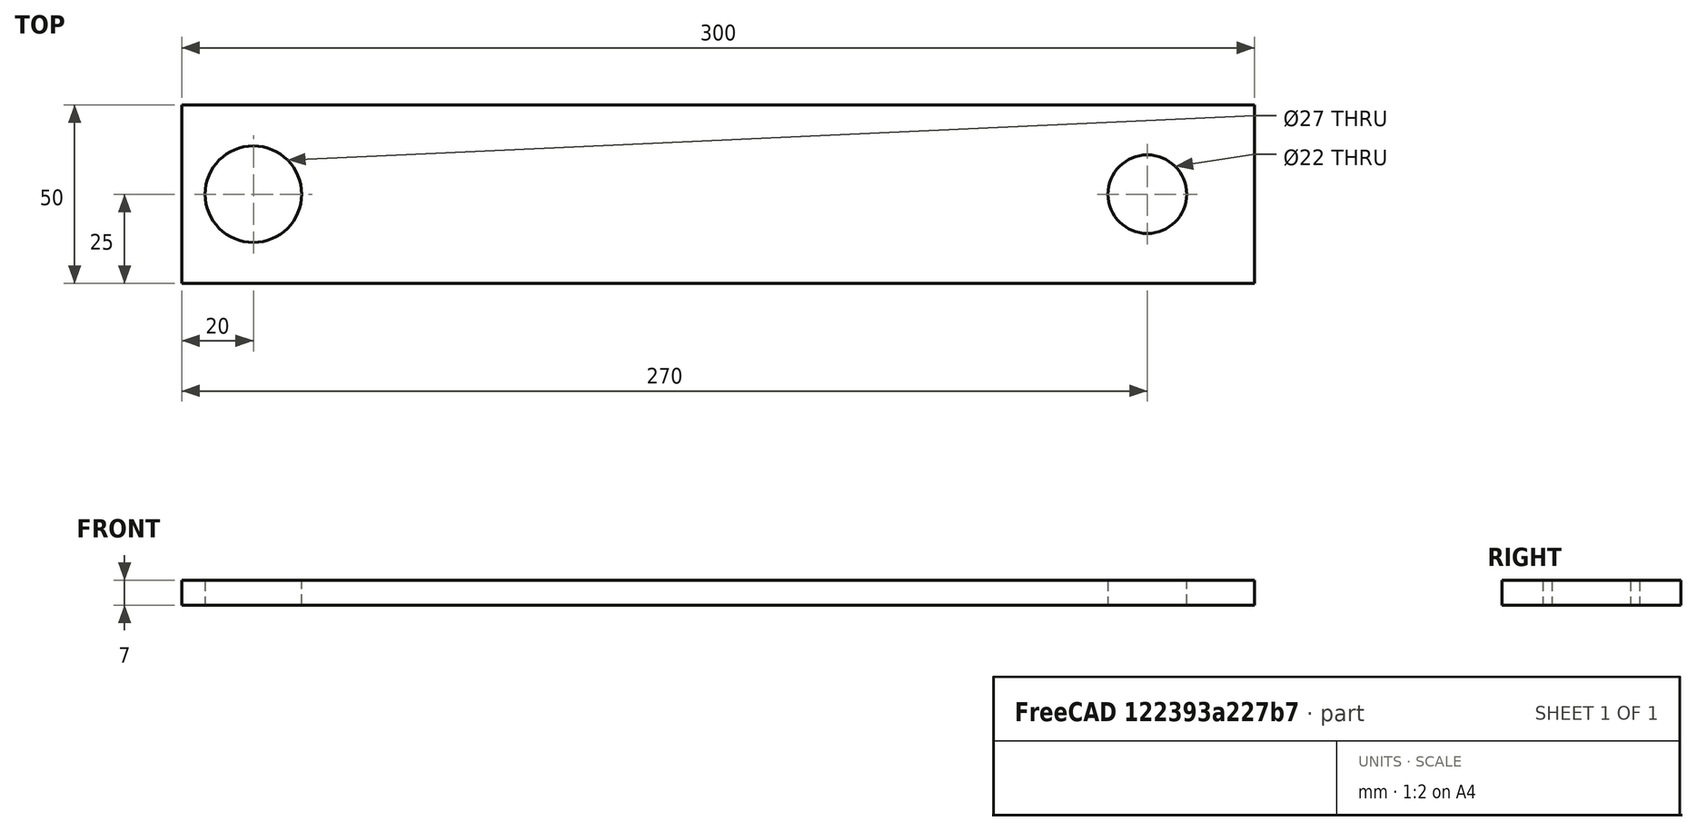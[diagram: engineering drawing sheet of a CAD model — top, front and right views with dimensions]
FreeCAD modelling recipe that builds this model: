
FCSTD DOCUMENT  (FreeCAD 0.19R24276 (Git))
Label: richag_300_d22_d27
License: All rights reserved
LicenseURL: http://en.wikipedia.org/wiki/All_rights_reserved
objects: Sketcher::SketchObject×1, PartDesign::Pad×1, PartDesign::Body×1
note: 4 computed .brp shape members not serialized (recipe doc carries the construction recipe); baked Part::Feature solids carry a one-line shape summary decoded from their .brp

FEATURE [Sketcher::SketchObject] Sketch
  FullyConstrained = true
  MapMode = 5
  Support = -> [XY_Plane]
  sketch-geometry (6):
    g0: Circle CenterX=0 CenterY=0 CenterZ=0 NormalX=0 NormalY=0 NormalZ=1 AngleXU=0 Radius=13.5
    g1: Circle CenterX=250 CenterY=0 CenterZ=0 NormalX=0 NormalY=0 NormalZ=1 AngleXU=0 Radius=11
    g2: LineSegment StartX=-20 StartY=25 StartZ=0 EndX=280 EndY=25 EndZ=0
    g3: LineSegment StartX=280 StartY=25 StartZ=0 EndX=280 EndY=-25 EndZ=0
    g4: LineSegment StartX=280 StartY=-25 StartZ=0 EndX=-20 EndY=-25 EndZ=0
    g5: LineSegment StartX=-20 StartY=-25 StartZ=0 EndX=-20 EndY=25 EndZ=0
  constraints (17):
    c: Coincident(g-1,g0)
    c: Diameter(g0) = 27
    c: PointOnObject(g1,g-1)
    c: Diameter(g1) = 22
    c: Coincident(g2,g3)
    c: Coincident(g3,g4)
    c: Coincident(g4,g5)
    c: Coincident(g5,g2)
    c: Horizontal(g2)
    c: Horizontal(g4)
    c: Vertical(g3)
    c: Vertical(g5)
    c: DistanceX(g4,g0) = 20
    c: DistanceX(g0,g1) = 250
    c: DistanceX(g4,g4) = 300
    c: DistanceY(g0,g2) = 25
    c: DistanceY(g4,g0) = 25
FEATURE [PartDesign::Pad] Pad
  Direction = (1,1,1)
  Length = 7
  Length2 = 100
  Profile = -> Sketch
  Type = 0
FEATURE [PartDesign::Body] Body
  Group = -> [Sketch,Pad]
  Origin = -> Origin
  Tip = -> Pad
